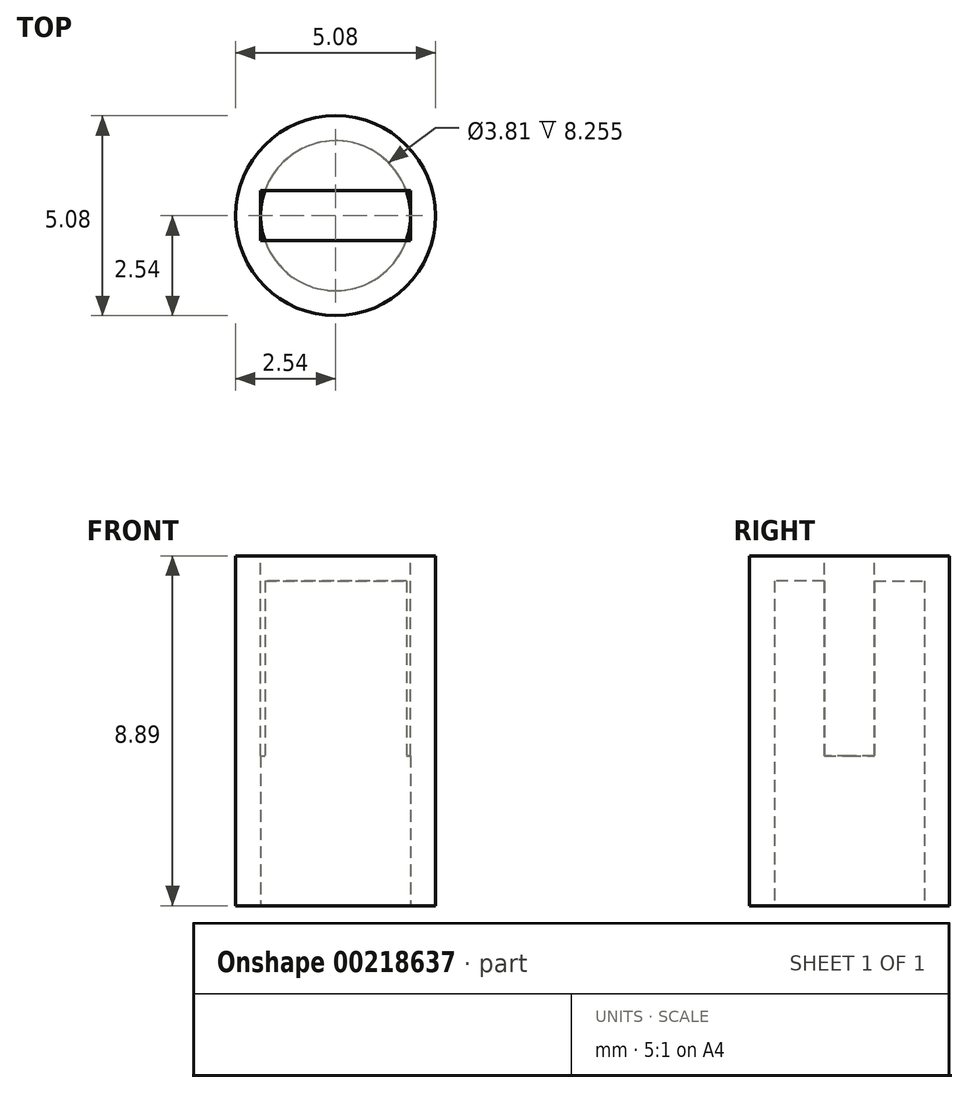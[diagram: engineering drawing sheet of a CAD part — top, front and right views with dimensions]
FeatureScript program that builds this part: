
annotation { "Feature Type Name" : "Feature", "Feature Type Description" : "" }
export const myFeature = defineFeature(function(context is Context, id is Id, definition is map)
    precondition{}
    {
        {
            var Q0;
            Q0=qCreatedBy(makeId("Top.planeOp"),FACE);
            var sketch = newSketch(context, id + "F0", { "sketchPlane" : qUnion([Q0])});
            skCircle(sketch, "E0", {"center": v(0, 0) * mm, "radius": 2.54 * mm});
            skSolve(sketch);
        }
        {
            var Q0;
            Q0=makeQuery(id+"F0.imprint","IMPRINT",FACE,{"disambiguationData":[TD([[makeQuery(id+"F0.imprint","IMPRINT",EDGE,{"derivedFrom":sQuery(id+"F0.wireOp",EDGE,"E0")}),1.0]])]});
            extrude(context, id + "F1", {"entities" : qUnion([Q0]), "depth" : 8.9 * mm});
        }
        {
            var Q0;
            Q0=makeQuery(id+"F1.opExtrude","CAP_FACE",FACE,{"disambiguationData":[OSD([sQuery(id+"F0.wireOp",EDGE,"E0")])],"isStart":true});
            shell(context, id + "F2", {"entities" : qUnion([Q0]), "thickness" : 0.64 * mm});
        }
        {
            var Q0;
            Q0=makeQuery(id+"F1.opExtrude","CAP_FACE",FACE,{"disambiguationData":[OSD([sQuery(id+"F0.wireOp",EDGE,"E0")])],"isStart":false});
            var sketch = newSketch(context, id + "F3", { "sketchPlane" : qUnion([Q0])});
            skLineSegment(sketch, "E1.bottom", {"start": v(-1.9, -0.64) * mm, "end": v(1.9, -0.64) * mm});
            skLineSegment(sketch, "E1.top", {"start": v(-1.9, 0.64) * mm, "end": v(1.9, 0.64) * mm});
            skLineSegment(sketch, "E1.left", {"start": v(-1.9, -0.64) * mm, "end": v(-1.9, 0.64) * mm});
            skLineSegment(sketch, "E1.right", {"start": v(1.9, -0.64) * mm, "end": v(1.9, 0.64) * mm});
            skPoint(sketch, "E2.startSnap0", {"position": v(0, 0.64) * mm});
            skLineSegment(sketch, "E3", {"start": v(-1.9, 0) * mm, "end": v(1.9, 0) * mm, "construction": true});
            skLineSegment(sketch, "E4", {"start": v(0, 0.64) * mm, "end": v(0, -0.64) * mm, "construction": true});
            skSolve(sketch);
        }
        {
            var Q0;
            Q0=makeQuery(id+"F3.imprint","IMPRINT",FACE,{"disambiguationData":[TD([[makeQuery(id+"F3.imprint","IMPRINT",EDGE,{"derivedFrom":sQuery(id+"F3.wireOp",EDGE,"E1.bottom")}),1.0]])]});
            extrude(context, id + "F4", {"entities" : qUnion([Q0]), "operationType" : NewBodyOperationType.REMOVE, "oppositeDirection" : true, "depth" : 5.08 * mm});
        }
    });
